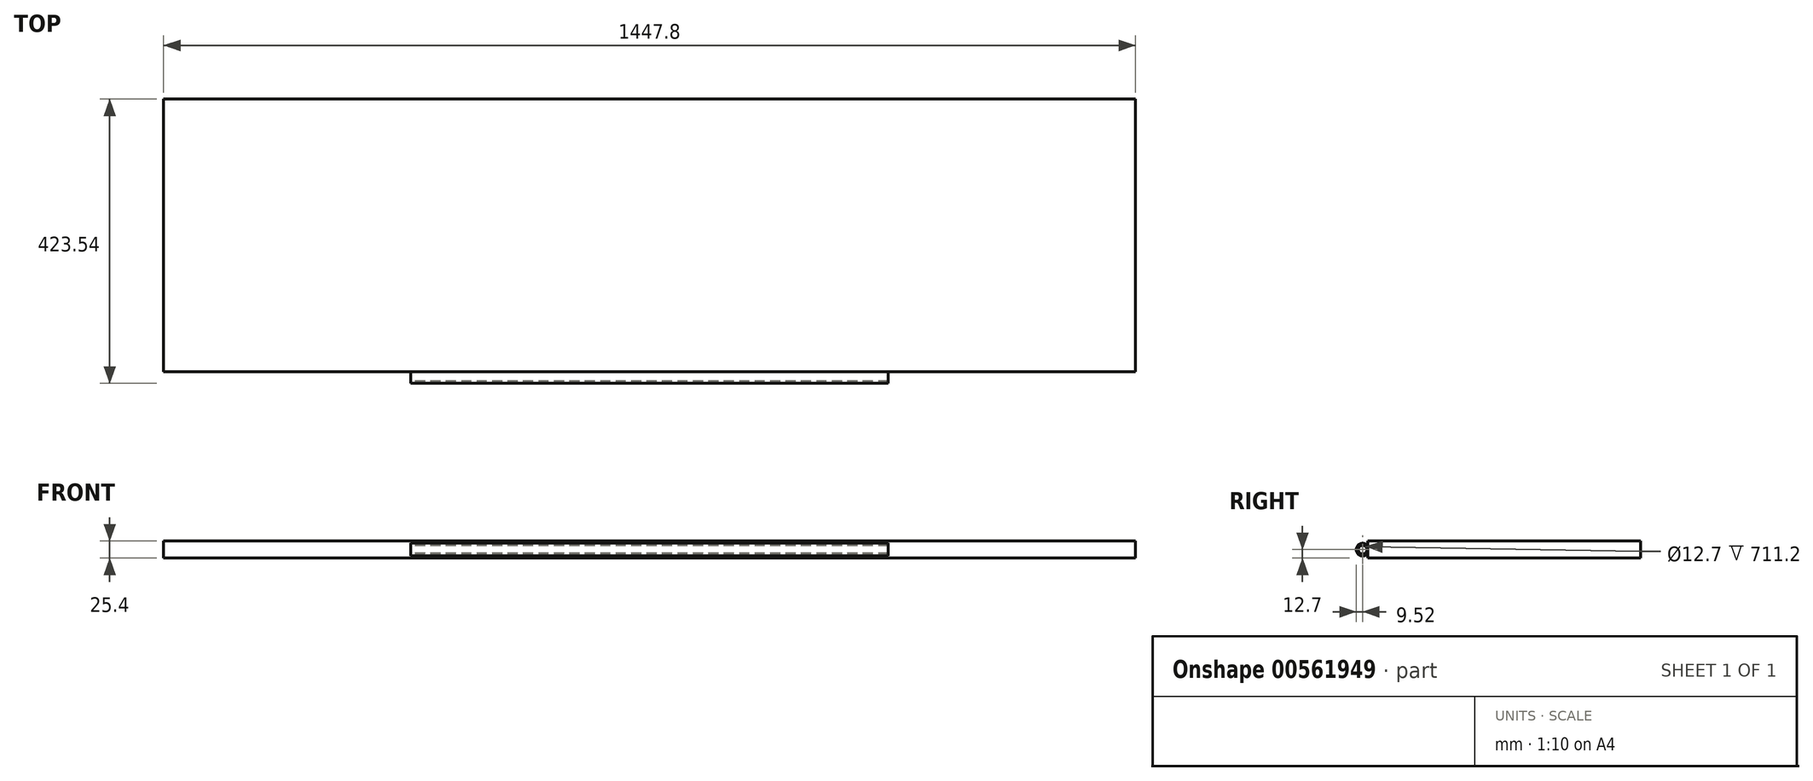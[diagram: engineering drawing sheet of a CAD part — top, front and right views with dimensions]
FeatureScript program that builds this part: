
annotation { "Feature Type Name" : "Feature", "Feature Type Description" : "" }
export const myFeature = defineFeature(function(context is Context, id is Id, definition is map)
    precondition{}
    {
        {
            var Q0;
            Q0=qCreatedBy(makeId("Top.planeOp"),FACE);
            var sketch = newSketch(context, id + "F0", { "sketchPlane" : qUnion([Q0])});
            skLineSegment(sketch, "E0.bottom", {"start": v(-723.9, -203.2) * mm, "end": v(723.9, -203.2) * mm});
            skLineSegment(sketch, "E0.top", {"start": v(-723.9, 203.2) * mm, "end": v(723.9, 203.2) * mm});
            skLineSegment(sketch, "E0.left", {"start": v(-723.9, -203.2) * mm, "end": v(-723.9, 203.2) * mm});
            skLineSegment(sketch, "E0.right", {"start": v(723.9, -203.2) * mm, "end": v(723.9, 203.2) * mm});
            skPoint(sketch, "E0.middle", {"position": v(0, 0) * mm});
            skSolve(sketch);
        }
        {
            var Q0;
            Q0=qCreatedBy(makeId("Right.planeOp"),FACE);
            var sketch = newSketch(context, id + "F1", { "sketchPlane" : qUnion([Q0])});
            skCircle(sketch, "E1", {"center": v(-210.82, 0) * mm, "radius": 6.35 * mm});
            skCircle(sketch, "E2", {"center": v(-210.82, 0) * mm, "radius": 9.53 * mm});
            skSolve(sketch);
        }
        {
            var Q0;
            Q0=makeQuery(id+"F0.imprint","IMPRINT",FACE,{"disambiguationData":[TD([[makeQuery(id+"F0.imprint","IMPRINT",EDGE,{"derivedFrom":sQuery(id+"F0.wireOp",EDGE,"E0.bottom")}),1.0]])]});
            extrude(context, id + "F2", {"entities" : qUnion([Q0]), "depth" : 25.4 * mm, "offsetDistance" : 25.4 * mm, "symmetric" : true});
        }
        {
            var Q0;
            Q0=makeQuery(id+"F1.imprint","IMPRINT",FACE,{"disambiguationData":[TD([[makeQuery(id+"F1.imprint","IMPRINT",EDGE,{"derivedFrom":sQuery(id+"F1.wireOp",EDGE,"E1")}),-1.0]])]});
            extrude(context, id + "F3", {"entities" : qUnion([Q0]), "operationType" : NewBodyOperationType.ADD, "depth" : 711.2 * mm, "offsetDistance" : 25.4 * mm, "symmetric" : true});
        }
    });
